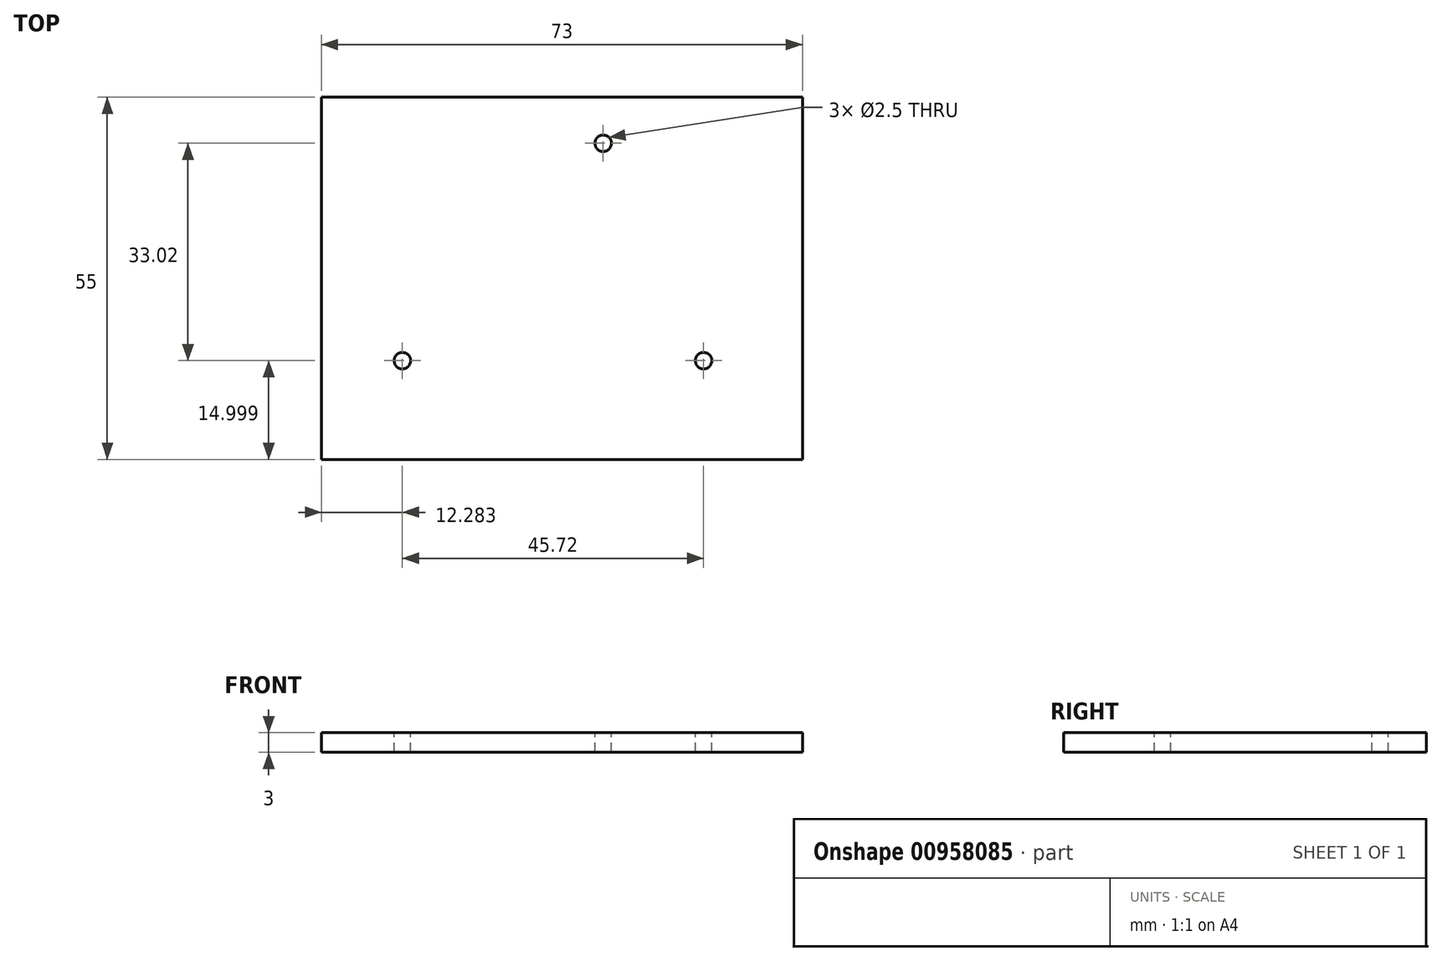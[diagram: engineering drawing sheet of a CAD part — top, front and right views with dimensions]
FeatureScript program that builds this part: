
annotation { "Feature Type Name" : "Feature", "Feature Type Description" : "" }
export const myFeature = defineFeature(function(context is Context, id is Id, definition is map)
    precondition{}
    {
        {
            var Q0;
            Q0=qCreatedBy(makeId("Top.planeOp"),FACE);
            var sketch = newSketch(context, id + "F0", { "sketchPlane" : qUnion([Q0])});
            skLineSegment(sketch, "E0.bottom", {"start": v(-18.64, 22.14) * mm, "end": v(54.36, 22.14) * mm});
            skLineSegment(sketch, "E0.top", {"start": v(-18.64, -32.86) * mm, "end": v(54.36, -32.86) * mm});
            skLineSegment(sketch, "E0.left", {"start": v(-18.64, 22.14) * mm, "end": v(-18.64, -32.86) * mm});
            skLineSegment(sketch, "E0.right", {"start": v(54.36, 22.14) * mm, "end": v(54.36, -32.86) * mm});
            skCircle(sketch, "E1", {"center": v(24.12, 15.16) * mm, "radius": 3.5 * mm});
            skCircle(sketch, "E2", {"center": v(24.12, 15.16) * mm, "radius": 1.25 * mm});
            skCircle(sketch, "E3", {"center": v(39.36, -17.86) * mm, "radius": 3.5 * mm});
            skCircle(sketch, "E4", {"center": v(39.36, -17.86) * mm, "radius": 1.25 * mm});
            skLineSegment(sketch, "E5", {"start": v(39.36, -21.36) * mm, "end": v(35.36, -21.36) * mm});
            skLineSegment(sketch, "E6", {"start": v(35.36, -13.36) * mm, "end": v(39.36, -13.36) * mm});
            skLineSegment(sketch, "E7", {"start": v(39.36, -13.36) * mm, "end": v(39.36, -14.36) * mm});
            skCircle(sketch, "E8.1.0.0", {"center": v(-6.36, -17.86) * mm, "radius": 3.5 * mm});
            skCircle(sketch, "E8.1.0.1", {"center": v(-6.36, -17.86) * mm, "radius": 1.25 * mm});
            skLineSegment(sketch, "E8.direction1", {"start": v(39.36, -17.86) * mm, "end": v(-6.36, -17.86) * mm, "construction": true});
            skSolve(sketch);
        }
        {
            var Q0;
            Q0=makeQuery(id+"F0.imprint","IMPRINT",FACE,{"disambiguationData":[TD([[makeQuery(id+"F0.imprint","IMPRINT",EDGE,{"derivedFrom":sQuery(id+"F0.wireOp",EDGE,"E0.bottom")}),-1.0]])]});
            var Q1;
            Q1=makeQuery(id+"F0.imprint","IMPRINT",FACE,{"disambiguationData":[TD([[makeQuery(id+"F0.imprint","IMPRINT",EDGE,{"derivedFrom":sQuery(id+"F0.wireOp",EDGE,"RPGhcm5J-WxrQ-m6qE-U7QP-122cDrHBgRUp")}),-1.0]])]});
            var Q2;
            Q2=makeQuery(id+"F0.imprint","IMPRINT",FACE,{"disambiguationData":[TD([[makeQuery(id+"F0.imprint","IMPRINT",EDGE,{"derivedFrom":sQuery(id+"F0.wireOp",EDGE,"d8NNWsW9-pKz7-konY-F6Ru-EoPawrHPcnrk")}),1.0]])]});
            var Q3;
            Q3=makeQuery(id+"F0.imprint","IMPRINT",FACE,{"disambiguationData":[TD([[makeQuery(id+"F0.imprint","IMPRINT",EDGE,{"derivedFrom":sQuery(id+"F0.wireOp",EDGE,"d8NNWsW9-pKz7-konY-F6Ru-EoPawrHPcnrk")}),-1.0]])]});
            var Q4;
            Q4=makeQuery(id+"F0.imprint","IMPRINT",FACE,{"disambiguationData":[TD([[makeQuery(id+"F0.imprint","IMPRINT",EDGE,{"derivedFrom":sQuery(id+"F0.wireOp",EDGE,"UIh1WeIG-55Ni-c0WG-7QqS-DhVz4KrpnhyC")}),1.0]])]});
            var Q5;
            Q5=makeQuery(id+"F0.imprint","IMPRINT",FACE,{"disambiguationData":[TD([[makeQuery(id+"F0.imprint","IMPRINT",EDGE,{"derivedFrom":sQuery(id+"F0.wireOp",EDGE,"UIh1WeIG-55Ni-c0WG-7QqS-DhVz4KrpnhyC")}),-1.0]])]});
            var Q6;
            Q6=makeQuery(id+"F0.imprint","IMPRINT",FACE,{"disambiguationData":[TD([[makeQuery(id+"F0.imprint","IMPRINT",EDGE,{"derivedFrom":sQuery(id+"F0.wireOp",EDGE,"QeMdJN8A-dn9j-3xki-fktR-3pxM612Ev0Hr")}),1.0]])]});
            var Q7;
            Q7=makeQuery(id+"F0.imprint","IMPRINT",FACE,{"disambiguationData":[TD([[makeQuery(id+"F0.imprint","IMPRINT",EDGE,{"derivedFrom":sQuery(id+"F0.wireOp",EDGE,"QeMdJN8A-dn9j-3xki-fktR-3pxM612Ev0Hr")}),-1.0]])]});
            var Q8;
            Q8=makeQuery(id+"F0.imprint","IMPRINT",FACE,{"disambiguationData":[TD([[makeQuery(id+"F0.imprint","IMPRINT",EDGE,{"derivedFrom":sQuery(id+"F0.wireOp",EDGE,"RPGhcm5J-WxrQ-m6qE-U7QP-122cDrHBgRUp")}),1.0]])]});
            var Q9;
            Q9=makeQuery(id+"F0.imprint","IMPRINT",FACE,{"disambiguationData":[TD([[makeQuery(id+"F0.imprint","IMPRINT",EDGE,{"derivedFrom":sQuery(id+"F0.wireOp",EDGE,"E1")}),1.0]])]});
            var Q10;
            Q10=makeQuery(id+"F0.imprint","IMPRINT",FACE,{"disambiguationData":[TD([[makeQuery(id+"F0.imprint","IMPRINT",EDGE,{"derivedFrom":sQuery(id+"F0.wireOp",EDGE,"q9TJ2LY5-POG3-TUHl-UAtc-KkXCwBF0dg0K")}),1.0]])]});
            var Q11;
            Q11=makeQuery(id+"F0.imprint","IMPRINT",FACE,{"disambiguationData":[TD([[makeQuery(id+"F0.imprint","IMPRINT",EDGE,{"derivedFrom":sQuery(id+"F0.wireOp",EDGE,"XiYqeTYE-pU58-1fM4-AqhE-TZQZLTUDdGxj")}),1.0]])]});
            var Q12;
            Q12=makeQuery(id+"F0.imprint","IMPRINT",FACE,{"disambiguationData":[TD([[makeQuery(id+"F0.imprint","IMPRINT",EDGE,{"derivedFrom":sQuery(id+"F0.wireOp",EDGE,"E3")}),1.0]])]});
            var Q13;
            Q13=makeQuery(id+"F0.imprint","IMPRINT",FACE,{"disambiguationData":[TD([[makeQuery(id+"F0.imprint","IMPRINT",EDGE,{"derivedFrom":sQuery(id+"F0.wireOp",EDGE,"7ujk2dRf-9cMt-fQ6i-N9Kf-E5Ec13K7eCMi")}),1.0]])]});
            var Q14;
            Q14=makeQuery(id+"F0.imprint","IMPRINT",FACE,{"disambiguationData":[TD([[makeQuery(id+"F0.imprint","IMPRINT",EDGE,{"derivedFrom":sQuery(id+"F0.wireOp",EDGE,"10X1w9HQ-WB88-kaE1-SOGO-IKVvKvK89rZx")}),1.0]])]});
            var Q15;
            {var subQ0=sQuery(id+"F0.wireOp",EDGE,"E5");Q15=makeQuery(id+"F0.imprint","IMPRINT",FACE,{"disambiguationData":[TD([[makeQuery(id+"F0.imprint","IMPRINT",EDGE,{"derivedFrom":subQ0}),-1.0]])]});}
            var Q16;
            {var subQ0=sQuery(id+"F0.wireOp",EDGE,"UazZci6k-yQEH-brCU-qpna-42nWtEBikQR3");Q16=makeQuery(id+"F0.imprint","IMPRINT",FACE,{"disambiguationData":[TD([[makeQuery(id+"F0.imprint","IMPRINT",EDGE,{"derivedFrom":subQ0}),1.0]])]});}
            var Q17;
            Q17=makeQuery(id+"F0.imprint","IMPRINT",FACE,{"disambiguationData":[TD([[makeQuery(id+"F0.imprint","IMPRINT",EDGE,{"derivedFrom":sQuery(id+"F0.wireOp",EDGE,"E8.1.0.0")}),1.0]])]});
            extrude(context, id + "F1", {"entities" : qUnion([Q0, Q1, Q2, Q3, Q4, Q5, Q6, Q7, Q8, Q9, Q10, Q11, Q12, Q13, Q14, Q15, Q16, Q17]), "oppositeDirection" : true, "depth" : 3 * mm, "offsetDistance" : 25 * mm});
        }
    });
